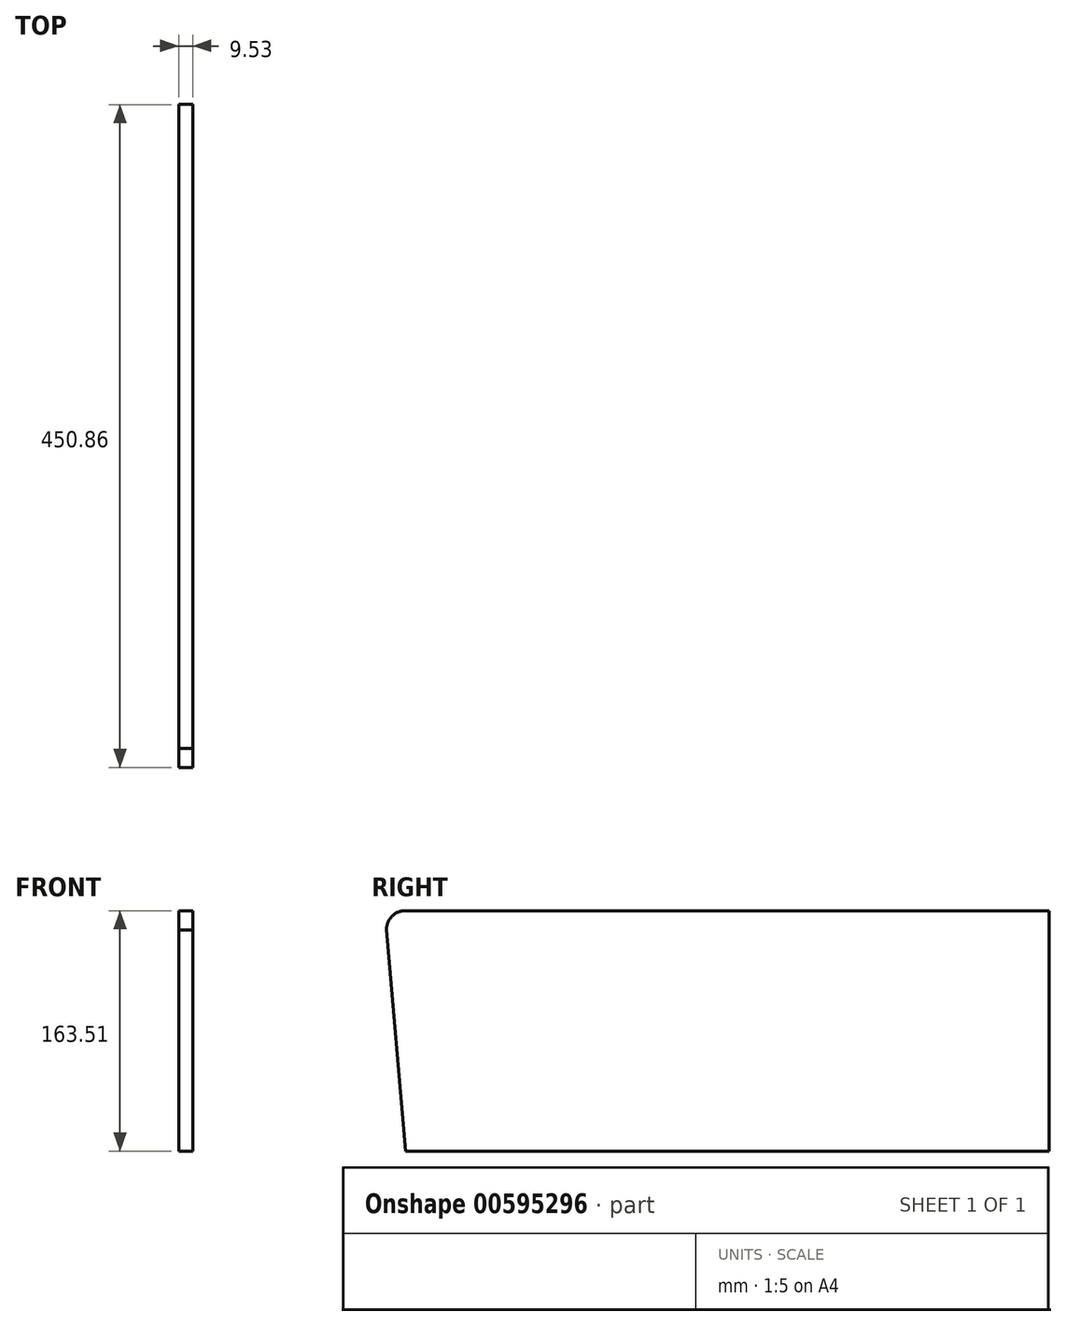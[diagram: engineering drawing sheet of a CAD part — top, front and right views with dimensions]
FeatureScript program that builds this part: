
annotation { "Feature Type Name" : "Feature", "Feature Type Description" : "" }
export const myFeature = defineFeature(function(context is Context, id is Id, definition is map)
    precondition{}
    {
        {
            var Q0;
            Q0=qCreatedBy(makeId("Right.planeOp"),FACE);
            var sketch = newSketch(context, id + "F0", { "sketchPlane" : qUnion([Q0])});
            skLineSegment(sketch, "E0", {"start": v(-91.37, -122.14) * mm, "end": v(-104.3, 28.14) * mm});
            skLineSegment(sketch, "E1", {"start": v(-91.3, 41.37) * mm, "end": v(346.55, 41.37) * mm});
            skArc(sketch, "E2", {"start": v(-91.3, 41.37) * mm, "mid": v(-100.67, 37.58) * mm, "end": v(-104.3, 28.14) * mm});
            skPoint(sketch, "E2.first.point", {"position": v(-104.3, 28.14) * mm});
            skPoint(sketch, "E2.second.point", {"position": v(-91.3, 41.37) * mm});
            skPoint(sketch, "E2.third.point", {"position": v(-85.77, 17.4) * mm});
            skLineSegment(sketch, "E3", {"start": v(-91.37, -122.14) * mm, "end": v(346.55, -122.14) * mm});
            skLineSegment(sketch, "E4", {"start": v(346.55, 41.37) * mm, "end": v(346.55, -122.14) * mm});
            skSolve(sketch);
        }
        {
            var Q0;
            Q0=makeQuery(id+"F0.imprint","IMPRINT",FACE,{"disambiguationData":[TD([[makeQuery(id+"F0.imprint","IMPRINT",EDGE,{"derivedFrom":sQuery(id+"F0.wireOp",EDGE,"E0")}),-1.0]])]});
            extrude(context, id + "F1", {"entities" : qUnion([Q0]), "depth" : 9.52 * mm, "offsetDistance" : 25.4 * mm});
        }
    });
